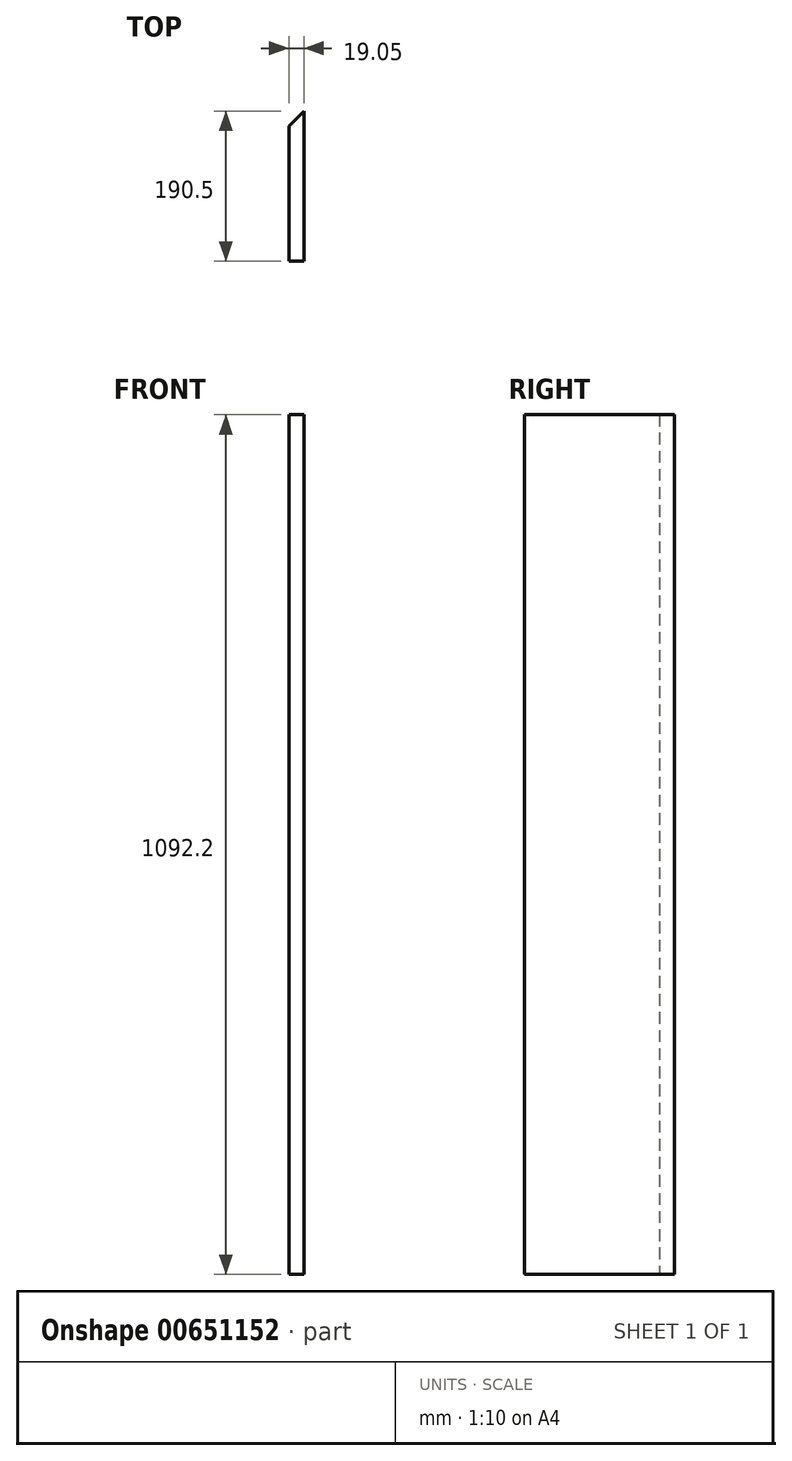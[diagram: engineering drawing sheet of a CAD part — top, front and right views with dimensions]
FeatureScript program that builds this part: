
annotation { "Feature Type Name" : "Feature", "Feature Type Description" : "" }
export const myFeature = defineFeature(function(context is Context, id is Id, definition is map)
    precondition{}
    {
        {
            var Q0;
            Q0=qCreatedBy(makeId("Right.planeOp"),FACE);
            var sketch = newSketch(context, id + "F0", { "sketchPlane" : qUnion([Q0])});
            skLineSegment(sketch, "E0.bottom", {"start": v(95.25, 546.1) * mm, "end": v(-95.25, 546.1) * mm});
            skLineSegment(sketch, "E0.top", {"start": v(95.25, -546.1) * mm, "end": v(-95.25, -546.1) * mm});
            skLineSegment(sketch, "E0.left", {"start": v(95.25, 546.1) * mm, "end": v(95.25, -546.1) * mm});
            skLineSegment(sketch, "E0.right", {"start": v(-95.25, 546.1) * mm, "end": v(-95.25, -546.1) * mm});
            skPoint(sketch, "E0.middle", {"position": v(0, 0) * mm});
            skSolve(sketch);
        }
        {
            var Q0;
            Q0=makeQuery(id+"F0.imprint","IMPRINT",FACE,{"disambiguationData":[TD([[makeQuery(id+"F0.imprint","IMPRINT",EDGE,{"derivedFrom":sQuery(id+"F0.wireOp",EDGE,"E0.bottom")}),1.0]])]});
            extrude(context, id + "F1", {"entities" : qUnion([Q0]), "depth" : 19.05 * mm, "offsetDistance" : 25.4 * mm});
        }
        {
            var Q0;
            Q0=makeQuery(id+"F1.opExtrude","CAP_EDGE",EDGE,{"disambiguationData":[OSD([sQuery(id+"F0.wireOp",EDGE,"E0.left")])],"isStart":true});
            chamfer(context, id + "F2", {"entities" : qUnion([Q0]), "width" : 19.05 * mm, "tangentPropagation" : true});
        }
    });
